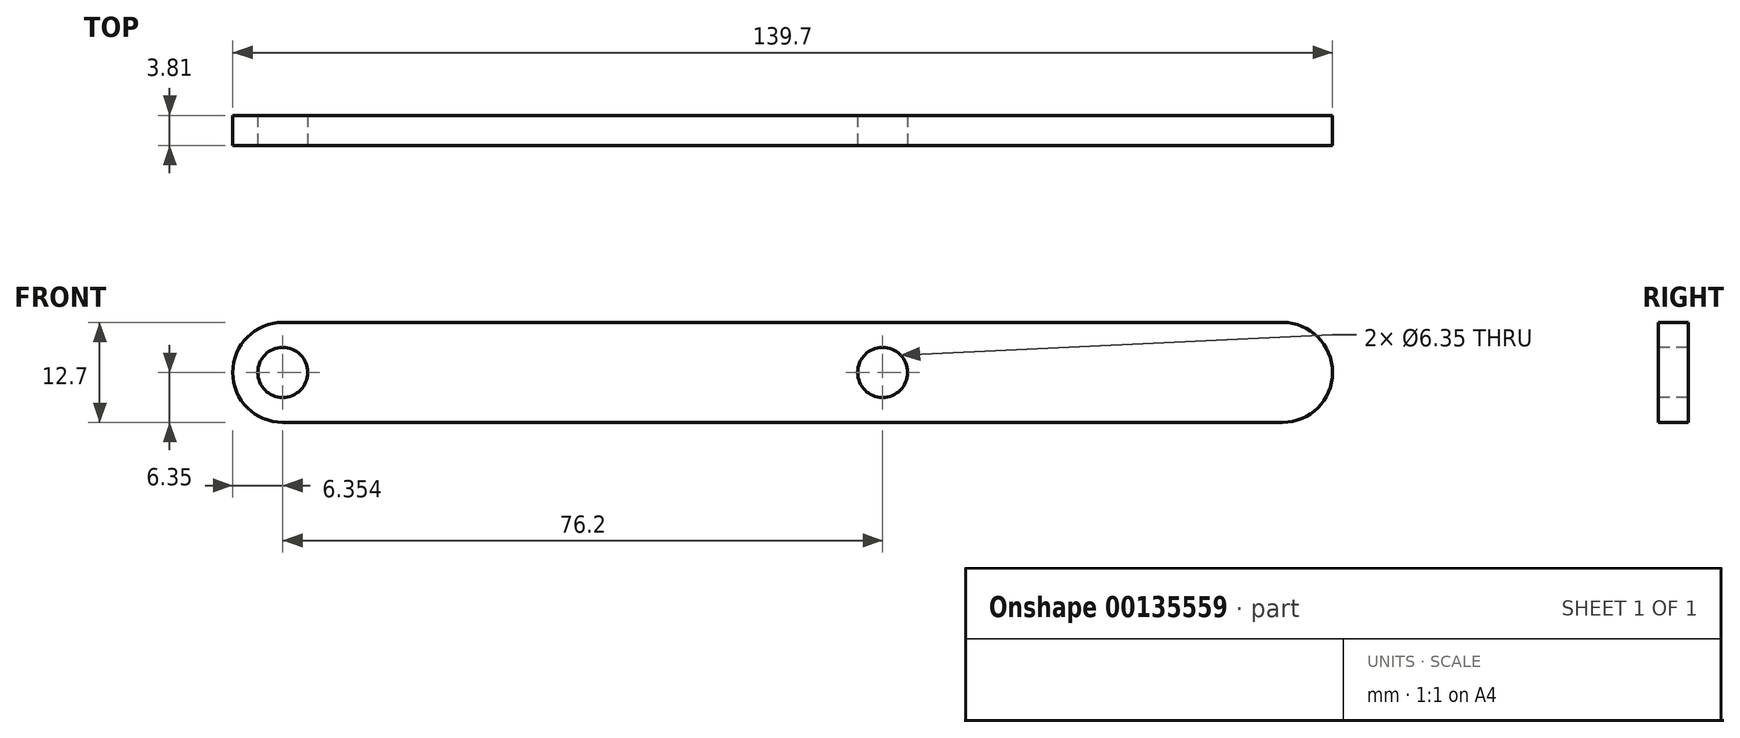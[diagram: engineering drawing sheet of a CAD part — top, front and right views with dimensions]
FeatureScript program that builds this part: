
annotation { "Feature Type Name" : "Feature", "Feature Type Description" : "" }
export const myFeature = defineFeature(function(context is Context, id is Id, definition is map)
    precondition{}
    {
        {
            var Q0;
            Q0=qCreatedBy(makeId("Front.planeOp"),FACE);
            var sketch = newSketch(context, id + "F0", { "sketchPlane" : qUnion([Q0])});
            skLineSegment(sketch, "E0", {"start": v(-75.3, 0) * mm, "end": v(51.7, 0) * mm});
            skLineSegment(sketch, "E1", {"start": v(-75.3, -12.7) * mm, "end": v(51.7, -12.7) * mm});
            skArc(sketch, "E2", {"start": v(51.7, -12.7) * mm, "mid": v(58.05, -6.35) * mm, "end": v(51.7, 0) * mm});
            skArc(sketch, "E3", {"start": v(-75.3, 0) * mm, "mid": v(-81.65, -6.35) * mm, "end": v(-75.3, -12.7) * mm});
            skSolve(sketch);
        }
        {
            var Q0;
            Q0=makeQuery(id+"F0.imprint","IMPRINT",FACE,{"disambiguationData":[TD([[makeQuery(id+"F0.imprint","IMPRINT",EDGE,{"derivedFrom":sQuery(id+"F0.wireOp",EDGE,"E0")}),-1.0]])]});
            extrude(context, id + "F1", {"entities" : qUnion([Q0]), "depth" : 3.8 * mm});
        }
        {
            var Q0;
            Q0=makeQuery(id+"F1.opExtrude","CAP_FACE",FACE,{"disambiguationData":[OSD([sQuery(id+"F0.wireOp",EDGE,"E0"),sQuery(id+"F0.wireOp",EDGE,"E1"),sQuery(id+"F0.wireOp",EDGE,"E2"),sQuery(id+"F0.wireOp",EDGE,"E3")])],"isStart":false});
            var sketch = newSketch(context, id + "F2", { "sketchPlane" : qUnion([Q0])});
            skCircle(sketch, "E4", {"center": v(-75.3, -6.35) * mm, "radius": 3.18 * mm});
            skCircle(sketch, "E5", {"center": v(0.9, -6.35) * mm, "radius": 3.18 * mm});
            skSolve(sketch);
        }
        {
            var Q0;
            Q0=makeQuery(id+"F2.imprint","IMPRINT",FACE,{"disambiguationData":[TD([[makeQuery(id+"F2.imprint","IMPRINT",EDGE,{"derivedFrom":sQuery(id+"F2.wireOp",EDGE,"E4")}),1.0]])]});
            var Q1;
            Q1=makeQuery(id+"F2.imprint","IMPRINT",FACE,{"disambiguationData":[TD([[makeQuery(id+"F2.imprint","IMPRINT",EDGE,{"derivedFrom":sQuery(id+"F2.wireOp",EDGE,"E5")}),1.0]])]});
            extrude(context, id + "F3", {"entities" : qUnion([Q0, Q1]), "operationType" : NewBodyOperationType.REMOVE, "oppositeDirection" : true, "depth" : 25.4 * mm});
        }
    });
